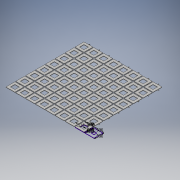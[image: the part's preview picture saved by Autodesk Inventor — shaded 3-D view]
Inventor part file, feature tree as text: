
AUTODESK INVENTOR PART (.ipt)
format: ipt  version: 2016 (Build 200138000, 138)  size: 844,800 bytes
history: native  units: in
note: dims shown in document units (in); Inventor stores cm internally (conversion verified against a paired STEP export)
features: extrude x4, pattern_linear x2, sketch x1, draft x1
ambient origin geometry x8: Origin, YZ Plane, XZ Plane, XY Plane, X Axis, Y Axis, Z Axis, Center Point
bodies: Solid1 (feature_tree)
feature tree (8):
  sketch  "Sketch1"  dims[d0=0.5in d1=0.5in d2=0.5in d3=0.5in d4=0.02in d5=0.0in d6=0.02in d7=0.0in d9=-0.0069in d10=0.01in d11=0.3436in d12=0.02in d13=0.02in d14=0.05in d15=3.1496in d17=0.55in d18=0.05in d21=0.3937in d23=0.0in d24=3.1496in d26=0.55in d27=0.175in d28=0.125in d29=0.0in d30=0.0in]
  extrude  "Extrusion1"  Depth=0.5in
  extrude  "Extrusion2"  Depth=0.5in
  draft  "FaceDraft2"
  extrude  "Extrusion4"  Depth=0.5in
  extrude  "Extrusion3"  Depth=0.02in TaperAngle=0.0deg
  pattern_linear  "Rectangular Pattern2"  Spacing1=0.02in  [1 undecoded]
  pattern_linear  "Rectangular Pattern1"  Spacing1=-0.0069in  [1 undecoded]
note: 2 required parameter values undecoded (feature->parameter linkage not recoverable at this tier; creation-order binding heuristic only, values carry confidence <= 0.55)
